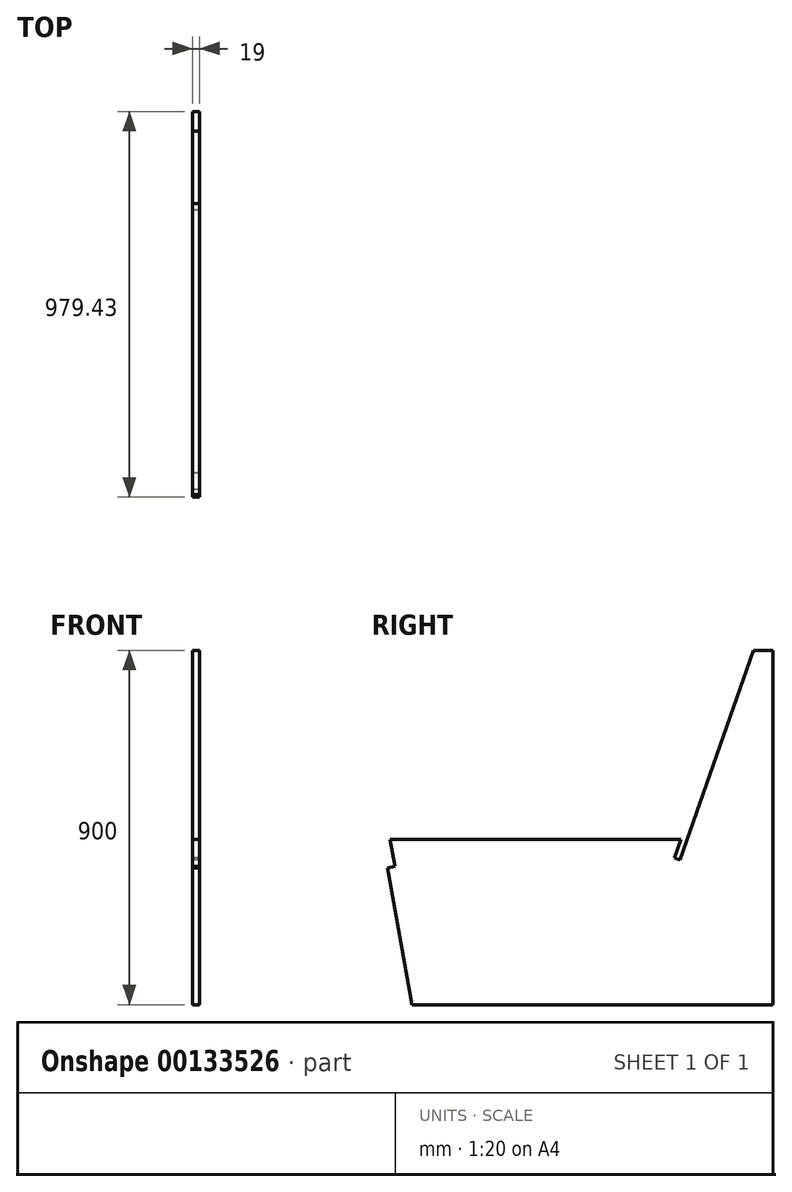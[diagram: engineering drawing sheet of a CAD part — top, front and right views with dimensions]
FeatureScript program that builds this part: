
annotation { "Feature Type Name" : "Feature", "Feature Type Description" : "" }
export const myFeature = defineFeature(function(context is Context, id is Id, definition is map)
    precondition{}
    {
        {
            var Q0;
            Q0=qCreatedBy(makeId("Right.planeOp"),FACE);
            var sketch = newSketch(context, id + "F0", { "sketchPlane" : qUnion([Q0])});
            skLineSegment(sketch, "E0", {"start": v(-979.43, 0) * mm, "end": v(0, 0) * mm});
            skLineSegment(sketch, "E1", {"start": v(0, 0) * mm, "end": v(0, 900) * mm});
            skLineSegment(sketch, "E2", {"start": v(0, 900) * mm, "end": v(-50, 900) * mm});
            skLineSegment(sketch, "E3", {"start": v(-251, 372.82) * mm, "end": v(-234.43, 420) * mm});
            skLineSegment(sketch, "E4", {"start": v(-234.43, 420) * mm, "end": v(-979.43, 420) * mm});
            skLineSegment(sketch, "E5", {"start": v(-979.43, 420) * mm, "end": v(-979.43, 0) * mm});
            skLineSegment(sketch, "E6", {"start": v(-251, 372.82) * mm, "end": v(-236.84, 367.85) * mm});
            skLineSegment(sketch, "E7", {"start": v(-236.84, 367.85) * mm, "end": v(-50, 900) * mm});
            skSolve(sketch);
        }
        {
            var Q0;
            Q0=makeQuery(id+"F0.imprint","IMPRINT",FACE,{"disambiguationData":[TD([[makeQuery(id+"F0.imprint","IMPRINT",EDGE,{"derivedFrom":sQuery(id+"F0.wireOp",EDGE,"E0")}),1.0]])]});
            extrude(context, id + "F1", {"entities" : qUnion([Q0]), "endBound" : BoundingType.SYMMETRIC, "depth" : 19 * mm});
        }
        {
            var Q0;
            Q0=makeQuery(id+"F1.opExtrude","CAP_FACE",FACE,{"disambiguationData":[OSD([sQuery(id+"F0.wireOp",EDGE,"E0"),sQuery(id+"F0.wireOp",EDGE,"E1"),sQuery(id+"F0.wireOp",EDGE,"E2"),sQuery(id+"F0.wireOp",EDGE,"E3"),sQuery(id+"F0.wireOp",EDGE,"E4"),sQuery(id+"F0.wireOp",EDGE,"E5"),sQuery(id+"F0.wireOp",EDGE,"E6"),sQuery(id+"F0.wireOp",EDGE,"E7")])],"isStart":true});
            var sketch = newSketch(context, id + "F2", { "sketchPlane" : qUnion([Q0])});
            skLineSegment(sketch, "E8", {"start": v(979.43, 347.76) * mm, "end": v(918.11, 0) * mm});
            skLineSegment(sketch, "E9", {"start": v(979.43, 347.76) * mm, "end": v(960.72, 351.06) * mm});
            skLineSegment(sketch, "E10", {"start": v(960.72, 351.06) * mm, "end": v(972.88, 420) * mm});
            skSolve(sketch);
        }
        {
            var Q0;
            {var subQ0=sQuery(id+"F2.wireOp",EDGE,"E8");Q0=makeQuery(id+"F2.imprint","IMPRINT",FACE,{"disambiguationData":[TD([[makeQuery(id+"F2.imprint","IMPRINT",EDGE,{"derivedFrom":subQ0}),1.0]])]});}
            var Q1;
            {var subQ0=sQuery(id+"F2.wireOp",EDGE,"E9");Q1=makeQuery(id+"F2.imprint","IMPRINT",FACE,{"disambiguationData":[TD([[makeQuery(id+"F2.imprint","IMPRINT",EDGE,{"derivedFrom":subQ0}),-1.0]])]});}
            extrude(context, id + "F3", {"entities" : qUnion([Q0, Q1]), "operationType" : NewBodyOperationType.REMOVE, "endBound" : BoundingType.THROUGH_ALL, "oppositeDirection" : true, "depth" : 25 * mm});
        }
    });
